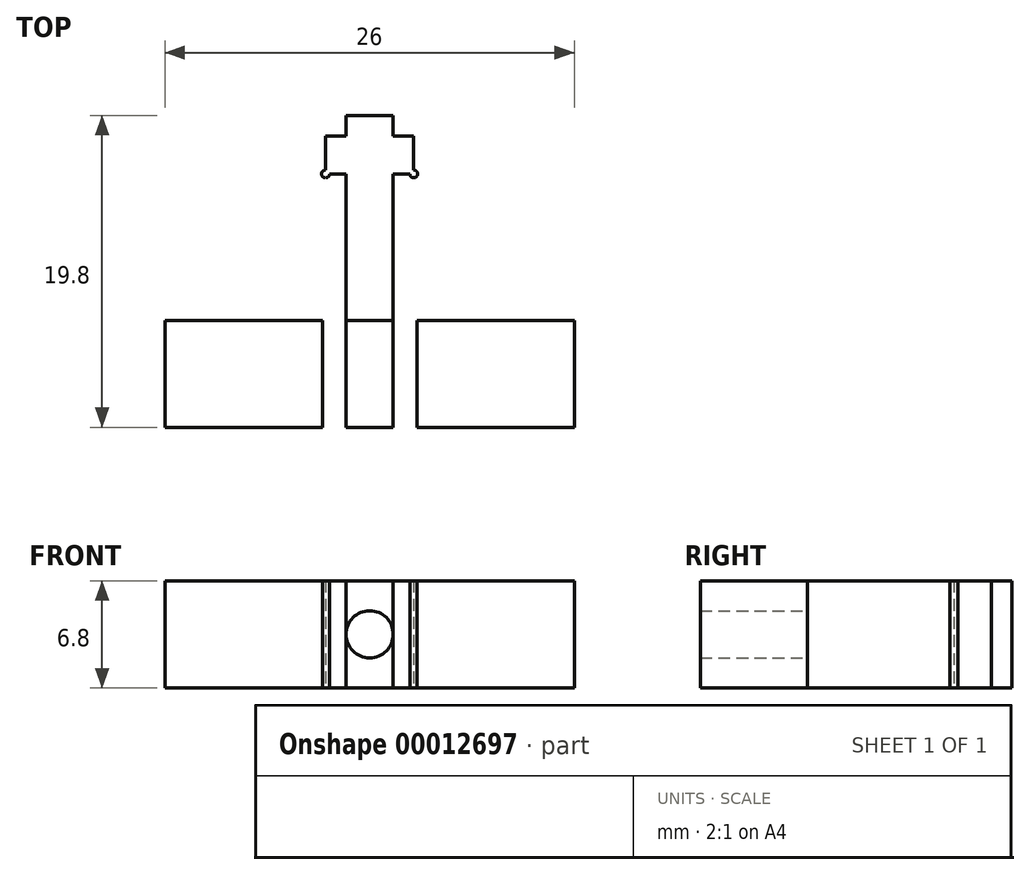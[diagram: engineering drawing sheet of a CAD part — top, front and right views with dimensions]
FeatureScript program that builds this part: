
annotation { "Feature Type Name" : "Feature", "Feature Type Description" : "" }
export const myFeature = defineFeature(function(context is Context, id is Id, definition is map)
    precondition{}
    {
        {
            var Q0;
            Q0=qCreatedBy(makeId("Top.planeOp"),FACE);
            var sketch = newSketch(context, id + "F0", { "sketchPlane" : qUnion([Q0])});
            skLineSegment(sketch, "E0", {"start": v(0, 0) * mm, "end": v(16.19, 0) * mm, "construction": true});
            skLineSegment(sketch, "E1", {"start": v(0, 0) * mm, "end": v(0, 13) * mm, "construction": true});
            skLineSegment(sketch, "E2", {"start": v(0, 13) * mm, "end": v(1.5, 13) * mm});
            skLineSegment(sketch, "E3", {"start": v(1.5, 13) * mm, "end": v(1.5, 0) * mm});
            skLineSegment(sketch, "E4", {"start": v(1.5, 0) * mm, "end": v(3, 0) * mm});
            skLineSegment(sketch, "E5", {"start": v(3, 0) * mm, "end": v(3, -6.8) * mm});
            skLineSegment(sketch, "E6", {"start": v(3, -6.8) * mm, "end": v(13, -6.8) * mm});
            skLineSegment(sketch, "E7", {"start": v(13, -6.8) * mm, "end": v(13, 0) * mm});
            skLineSegment(sketch, "E8", {"start": v(13, 0) * mm, "end": v(3, 0) * mm});
            skLineSegment(sketch, "E9", {"start": v(1.5, 0) * mm, "end": v(0, 0) * mm});
            skLineSegment(sketch, "E10", {"start": v(0, 9.3) * mm, "end": v(2.8, 9.3) * mm});
            skLineSegment(sketch, "E11", {"start": v(2.8, 9.3) * mm, "end": v(2.8, 11.7) * mm});
            skLineSegment(sketch, "E12", {"start": v(2.8, 11.7) * mm, "end": v(0, 11.7) * mm});
            skLineSegment(sketch, "E13.0.MirrorCS", {"start": v(0, 13) * mm, "end": v(-1.5, 13) * mm});
            skLineSegment(sketch, "E13.1.MirrorCS", {"start": v(-2.8, 11.7) * mm, "end": v(0, 11.7) * mm});
            skLineSegment(sketch, "E13.2.MirrorCS", {"start": v(-2.8, 9.3) * mm, "end": v(-2.8, 11.7) * mm});
            skLineSegment(sketch, "E13.3.MirrorCS", {"start": v(0, 9.3) * mm, "end": v(-2.8, 9.3) * mm});
            skLineSegment(sketch, "E13.4.MirrorCS", {"start": v(-1.5, 0) * mm, "end": v(0, 0) * mm});
            skLineSegment(sketch, "E13.5.MirrorCS", {"start": v(-1.5, 13) * mm, "end": v(-1.5, 0) * mm});
            skLineSegment(sketch, "E14.0.MirrorCS", {"start": v(-3, 0) * mm, "end": v(-3, -6.8) * mm});
            skLineSegment(sketch, "E15.0.MirrorCS", {"start": v(-3, -6.8) * mm, "end": v(-13, -6.8) * mm});
            skLineSegment(sketch, "E16.0.MirrorCS", {"start": v(-13, -6.8) * mm, "end": v(-13, 0) * mm});
            skLineSegment(sketch, "E17.0.MirrorCS", {"start": v(-13, 0) * mm, "end": v(-3, 0) * mm});
            skCircle(sketch, "E18", {"center": v(2.8, 9.3) * mm, "radius": 0.25 * mm});
            skCircle(sketch, "E19.0.MirrorC", {"center": v(-2.8, 9.3) * mm, "radius": 0.25 * mm});
            skSolve(sketch);
        }
        {
            var Q0;
            Q0=qCreatedBy(makeId("Front.planeOp"),FACE);
            var sketch = newSketch(context, id + "F1", { "sketchPlane" : qUnion([Q0])});
            skPoint(sketch, "E20.0", {"position": v(3, 0) * mm});
            skPoint(sketch, "E21.0", {"position": v(13, 0) * mm});
            skLineSegment(sketch, "E22", {"start": v(0, 0) * mm, "end": v(0, 6.8) * mm, "construction": true});
            skLineSegment(sketch, "E23", {"start": v(13, 0) * mm, "end": v(3, 0) * mm});
            skLineSegment(sketch, "E24", {"start": v(3, 0) * mm, "end": v(3, 6.8) * mm});
            skLineSegment(sketch, "E25", {"start": v(3, 6.8) * mm, "end": v(13, 6.8) * mm});
            skLineSegment(sketch, "E26", {"start": v(13, 6.8) * mm, "end": v(13, 0) * mm});
            skLineSegment(sketch, "E27", {"start": v(3, 6.8) * mm, "end": v(0, 6.8) * mm, "construction": true});
            skCircle(sketch, "E28", {"center": v(0, 3.4) * mm, "radius": 1.5 * mm});
            skLineSegment(sketch, "E29.0.MirrorCS", {"start": v(-3, 0) * mm, "end": v(-3, 6.8) * mm});
            skLineSegment(sketch, "E29.1.MirrorCS", {"start": v(-13, 0) * mm, "end": v(-3, 0) * mm});
            skLineSegment(sketch, "E29.2.MirrorCS", {"start": v(-13, 6.8) * mm, "end": v(-13, 0) * mm});
            skLineSegment(sketch, "E29.3.MirrorCS", {"start": v(-3, 6.8) * mm, "end": v(-13, 6.8) * mm});
            skSolve(sketch);
        }
        {
            var Q0;
            {var subQ3=sQuery(id+"F0.wireOp",EDGE,"E13.2.MirrorCS");var subQ7=sQuery(id+"F0.wireOp",EDGE,"E13.1.MirrorCS");var subQ9=makeQuery(id+"F0.imprint","INTERSECT",VERTEX,{"derivedFrom":[subQ7,subQ3]});Q0=makeQuery(id+"F0.imprint","IMPRINT",FACE,{"disambiguationData":[TD([[makeQuery(id+"F0.imprint","IMPRINT",EDGE,{"disambiguationData":[TD([[subQ9,-1.0]])],"derivedFrom":subQ7}),-1.0]])]});}
            var Q1;
            {var subQ8=sQuery(id+"F0.wireOp",EDGE,"E2");Q1=makeQuery(id+"F0.imprint","IMPRINT",FACE,{"disambiguationData":[TD([[makeQuery(id+"F0.imprint","IMPRINT",EDGE,{"derivedFrom":subQ8}),-1.0]])]});}
            var Q2;
            {var subQ7=sQuery(id+"F0.wireOp",EDGE,"E12");var subQ9=sQuery(id+"F0.wireOp",EDGE,"E3");var subQ10=makeQuery(id+"F0.imprint","INTERSECT",VERTEX,{"derivedFrom":[subQ9,subQ7]});Q2=makeQuery(id+"F0.imprint","IMPRINT",FACE,{"disambiguationData":[TD([[makeQuery(id+"F0.imprint","IMPRINT",EDGE,{"disambiguationData":[TD([[subQ10,-1.0]])],"derivedFrom":subQ9}),-1.0]])]});}
            var Q3;
            {var subQ8=sQuery(id+"F0.wireOp",EDGE,"E9");Q3=makeQuery(id+"F0.imprint","IMPRINT",FACE,{"disambiguationData":[TD([[makeQuery(id+"F0.imprint","IMPRINT",EDGE,{"derivedFrom":subQ8}),-1.0]])]});}
            var Q4;
            {var subQ5=sQuery(id+"F0.wireOp",EDGE,"E12");var subQ6=sQuery(id+"F0.wireOp",EDGE,"E3");var subQ7=makeQuery(id+"F0.imprint","INTERSECT",VERTEX,{"derivedFrom":[subQ6,subQ5]});Q4=makeQuery(id+"F0.imprint","IMPRINT",FACE,{"disambiguationData":[TD([[makeQuery(id+"F0.imprint","IMPRINT",EDGE,{"disambiguationData":[TD([[subQ7,-1.0]])],"derivedFrom":subQ6}),1.0]])]});}
            var Q5;
            {var subQ1=sQuery(id+"F0.wireOp",EDGE,"E11");var subQ3=sQuery(id+"F0.wireOp",EDGE,"E10");var subQ5=makeQuery(id+"F0.imprint","INTERSECT",VERTEX,{"derivedFrom":[subQ3,subQ1]});Q5=makeQuery(id+"F0.imprint","IMPRINT",FACE,{"disambiguationData":[TD([[makeQuery(id+"F0.imprint","IMPRINT",EDGE,{"disambiguationData":[TD([[subQ5,1.0]])],"derivedFrom":subQ3}),1.0]])]});}
            var Q6;
            {var subQ1=sQuery(id+"F0.wireOp",EDGE,"E13.3.MirrorCS");var subQ3=sQuery(id+"F0.wireOp",EDGE,"E13.2.MirrorCS");var subQ5=makeQuery(id+"F0.imprint","INTERSECT",VERTEX,{"derivedFrom":[subQ3,subQ1]});Q6=makeQuery(id+"F0.imprint","IMPRINT",FACE,{"disambiguationData":[TD([[makeQuery(id+"F0.imprint","IMPRINT",EDGE,{"disambiguationData":[TD([[subQ5,-1.0]])],"derivedFrom":subQ3}),-1.0]])]});}
            var Q7;
            {var subQ1=sQuery(id+"F0.wireOp",EDGE,"E11");var subQ3=sQuery(id+"F0.wireOp",EDGE,"E10");var subQ5=makeQuery(id+"F0.imprint","INTERSECT",VERTEX,{"derivedFrom":[subQ3,subQ1]});Q7=makeQuery(id+"F0.imprint","IMPRINT",FACE,{"disambiguationData":[TD([[makeQuery(id+"F0.imprint","IMPRINT",EDGE,{"disambiguationData":[TD([[subQ5,1.0]])],"derivedFrom":subQ3}),-1.0]])]});}
            var Q8;
            {var subQ1=sQuery(id+"F0.wireOp",EDGE,"E13.3.MirrorCS");var subQ3=sQuery(id+"F0.wireOp",EDGE,"E13.2.MirrorCS");var subQ5=makeQuery(id+"F0.imprint","INTERSECT",VERTEX,{"derivedFrom":[subQ3,subQ1]});Q8=makeQuery(id+"F0.imprint","IMPRINT",FACE,{"disambiguationData":[TD([[makeQuery(id+"F0.imprint","IMPRINT",EDGE,{"disambiguationData":[TD([[subQ5,-1.0]])],"derivedFrom":subQ3}),1.0]])]});}
            extrude(context, id + "F2", {"entities" : qUnion([Q0, Q1, Q2, Q3, Q4, Q5, Q6, Q7, Q8]), "depth" : 6.8 * mm});
        }
        {
            var Q0;
            Q0=makeQuery(id+"F0.imprint","IMPRINT",FACE,{"disambiguationData":[TD([[makeQuery(id+"F0.imprint","IMPRINT",EDGE,{"derivedFrom":sQuery(id+"F0.wireOp",EDGE,"E14.0.MirrorCS")}),-1.0]])]});
            var Q1;
            Q1=makeQuery(id+"F0.imprint","IMPRINT",FACE,{"disambiguationData":[TD([[makeQuery(id+"F0.imprint","IMPRINT",EDGE,{"derivedFrom":sQuery(id+"F0.wireOp",EDGE,"E5")}),1.0]])]});
            extrude(context, id + "F3", {"entities" : qUnion([Q0, Q1]), "depth" : 6.8 * mm});
        }
        {
            var Q0;
            Q0 = qSketchRegion(id + "F1", true);
            extrude(context, id + "F4", {"entities" : qUnion([Q0]), "depth" : 6.8 * mm});
        }
    });
